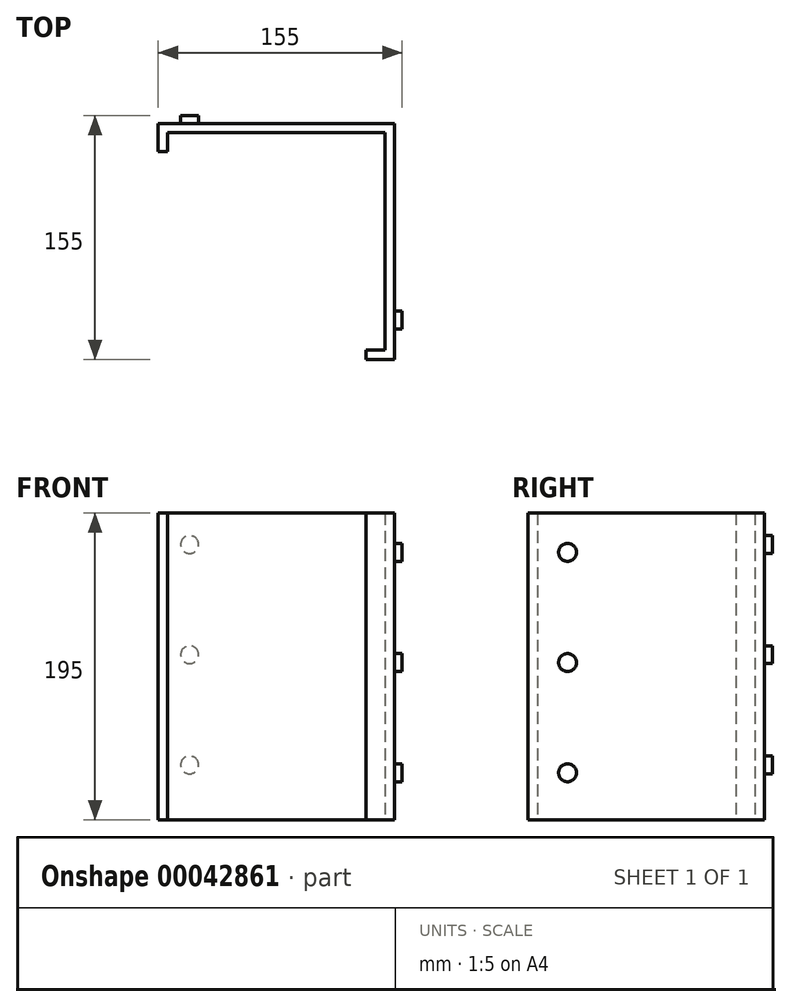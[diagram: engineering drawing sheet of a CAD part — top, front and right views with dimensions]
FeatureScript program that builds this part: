
annotation { "Feature Type Name" : "Feature", "Feature Type Description" : "" }
export const myFeature = defineFeature(function(context is Context, id is Id, definition is map)
    precondition{}
    {
        {
            var Q0;
            Q0=qCreatedBy(makeId("Top.planeOp"),FACE);
            var sketch = newSketch(context, id + "F0", { "sketchPlane" : qUnion([Q0])});
            skLineSegment(sketch, "E0", {"start": v(-74.95, 83.91) * mm, "end": v(-74.95, 65.91) * mm});
            skLineSegment(sketch, "E1", {"start": v(-68.95, 77.91) * mm, "end": v(69.05, 77.91) * mm});
            skLineSegment(sketch, "E2", {"start": v(69.05, 77.91) * mm, "end": v(69.05, -60.09) * mm});
            skLineSegment(sketch, "E3", {"start": v(75.05, -66.09) * mm, "end": v(75.05, 83.91) * mm});
            skLineSegment(sketch, "E4", {"start": v(75.05, 83.91) * mm, "end": v(-74.95, 83.91) * mm});
            skLineSegment(sketch, "E5", {"start": v(-74.95, 65.91) * mm, "end": v(-68.95, 65.91) * mm});
            skLineSegment(sketch, "E6", {"start": v(-68.95, 65.91) * mm, "end": v(-68.95, 77.91) * mm});
            skLineSegment(sketch, "E7", {"start": v(75.05, -66.09) * mm, "end": v(57.05, -66.09) * mm});
            skLineSegment(sketch, "E8", {"start": v(57.05, -66.09) * mm, "end": v(57.05, -60.09) * mm});
            skLineSegment(sketch, "E9", {"start": v(57.05, -60.09) * mm, "end": v(69.05, -60.09) * mm});
            skSolve(sketch);
        }
        {
            var Q0;
            Q0 = qSketchRegion(id + "F0", true);
            extrude(context, id + "F1", {"entities" : qUnion([Q0]), "depth" : 195 * mm});
        }
        {
            var Q0;
            Q0=makeQuery(id+"F1.opExtrude","SWEPT_FACE",FACE,{"disambiguationData":[OSD([sQuery(id+"F0.wireOp",EDGE,"E3")])]});
            var sketch = newSketch(context, id + "F2", { "sketchPlane" : qUnion([Q0])});
            skCircle(sketch, "E10", {"center": v(-41.09, 170) * mm, "radius": 5.68 * mm});
            skCircle(sketch, "E11.0.1.0", {"center": v(-41.09, 100) * mm, "radius": 5.68 * mm});
            skCircle(sketch, "E11.0.2.0", {"center": v(-41.09, 30) * mm, "radius": 5.68 * mm});
            skLineSegment(sketch, "E11.direction1", {"start": v(-41.09, 170) * mm, "end": v(-21, 170) * mm, "construction": true});
            skLineSegment(sketch, "E11.direction2", {"start": v(-41.09, 170) * mm, "end": v(-41.09, 100) * mm, "construction": true});
            skSolve(sketch);
        }
        {
            var Q0;
            Q0 = qSketchRegion(id + "F2", true);
            extrude(context, id + "F3", {"entities" : qUnion([Q0]), "operationType" : NewBodyOperationType.ADD, "depth" : 5 * mm});
        }
        {
            var Q0;
            Q0=makeQuery(id+"F1.opExtrude","SWEPT_FACE",FACE,{"disambiguationData":[OSD([sQuery(id+"F0.wireOp",EDGE,"E4")])]});
            var sketch = newSketch(context, id + "F4", { "sketchPlane" : qUnion([Q0])});
            skCircle(sketch, "E12", {"center": v(54.95, 175) * mm, "radius": 5.68 * mm});
            skCircle(sketch, "E13.0.1.0", {"center": v(54.95, 105) * mm, "radius": 5.68 * mm});
            skCircle(sketch, "E13.0.2.0", {"center": v(54.95, 35) * mm, "radius": 5.68 * mm});
            skLineSegment(sketch, "E13.direction1", {"start": v(-25.7, 175) * mm, "end": v(54.95, 175) * mm, "construction": true});
            skLineSegment(sketch, "E13.direction2", {"start": v(54.95, 175) * mm, "end": v(54.95, 105) * mm, "construction": true});
            skSolve(sketch);
        }
        {
            var Q0;
            Q0 = qSketchRegion(id + "F4", true);
            extrude(context, id + "F5", {"entities" : qUnion([Q0]), "operationType" : NewBodyOperationType.ADD, "depth" : 5 * mm});
        }
    });
